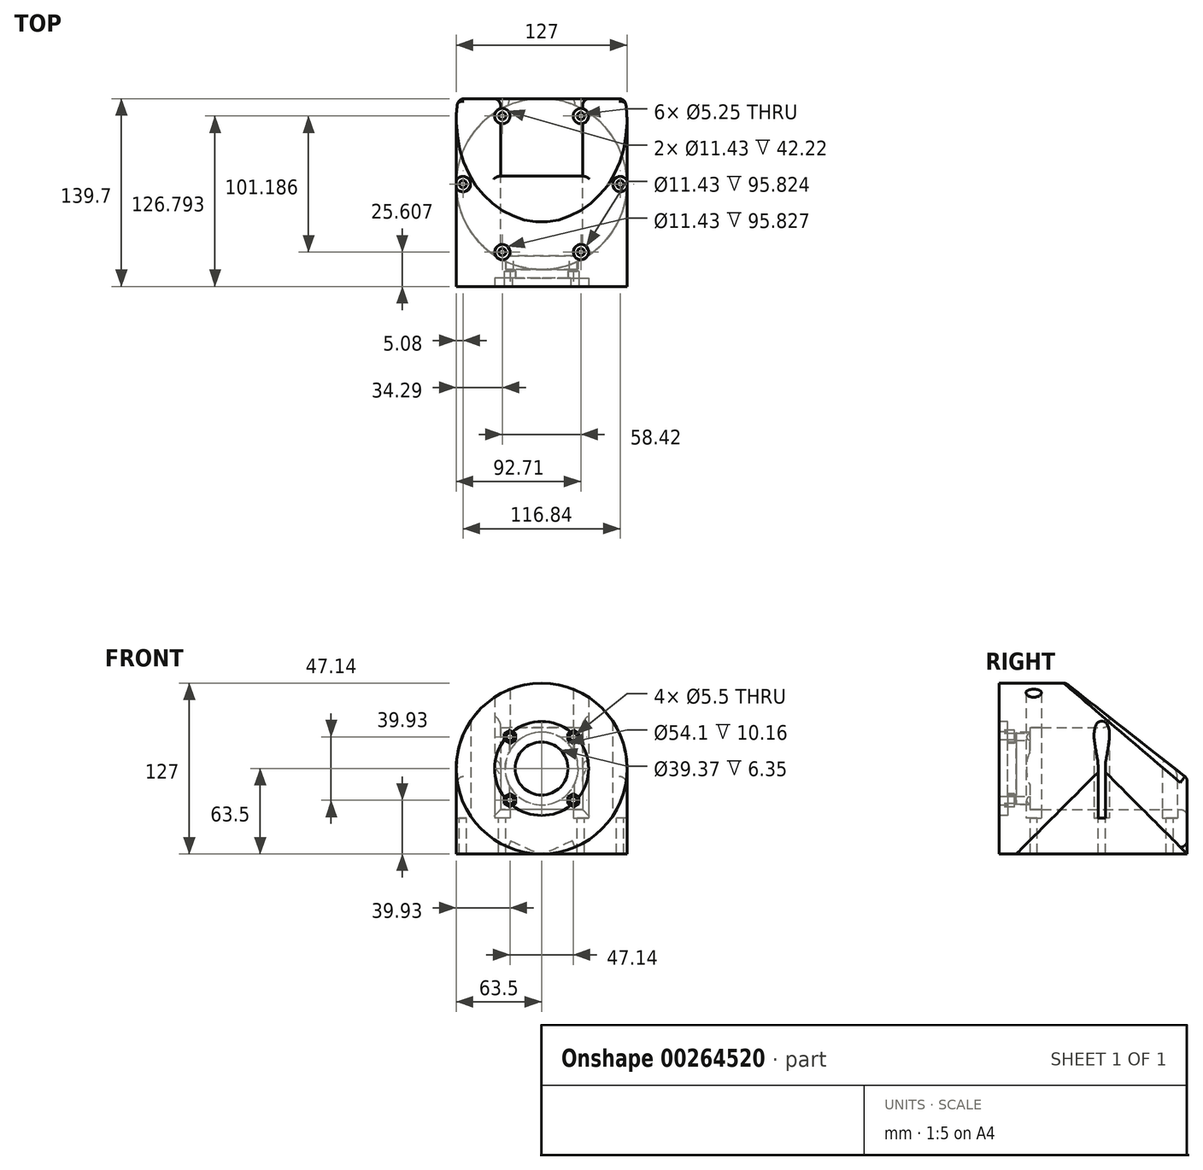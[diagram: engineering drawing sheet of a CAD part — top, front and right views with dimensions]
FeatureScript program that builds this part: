
annotation { "Feature Type Name" : "Feature", "Feature Type Description" : "" }
export const myFeature = defineFeature(function(context is Context, id is Id, definition is map)
    precondition{}
    {
        {
            var Q0;
            Q0=qCreatedBy(makeId("Front.planeOp"),FACE);
            var sketch = newSketch(context, id + "F0", { "sketchPlane" : qUnion([Q0])});
            skCircle(sketch, "E0", {"center": v(0, 0) * mm, "radius": 63.5 * mm});
            skSolve(sketch);
        }
        {
            var Q0;
            Q0 = qSketchRegion(id + "F0", true);
            extrude(context, id + "F1", {"entities" : qUnion([Q0]), "depth" : 76.2 * mm, "hasSecondDirection" : true, "secondDirectionOppositeDirection" : true, "secondDirectionDepth" : 63.5 * mm});
        }
        {
            var Q0;
            Q0=qCreatedBy(makeId("Top.planeOp"),FACE);
            var sketch = newSketch(context, id + "F2", { "sketchPlane" : qUnion([Q0])});
            skCircle(sketch, "E1", {"center": v(0, 0) * mm, "radius": 63.5 * mm});
            skSolve(sketch);
        }
        {
            var Q0;
            Q0 = qSketchRegion(id + "F2", true);
            extrude(context, id + "F3", {"entities" : qUnion([Q0]), "operationType" : NewBodyOperationType.ADD, "oppositeDirection" : true, "depth" : 63.5 * mm});
        }
        {
            var Q0;
            Q0=makeQuery(id+"F1.opExtrude","CAP_FACE",FACE,{"disambiguationData":[OSD([sQuery(id+"F0.wireOp",EDGE,"E0")])],"isStart":true});
            var sketch = newSketch(context, id + "F4", { "sketchPlane" : qUnion([Q0])});
            skLineSegment(sketch, "E2.bottom", {"start": v(-30.48, 30.48) * mm, "end": v(30.48, 30.48) * mm});
            skLineSegment(sketch, "E2.top", {"start": v(-30.48, -30.48) * mm, "end": v(30.48, -30.48) * mm});
            skLineSegment(sketch, "E2.left", {"start": v(-30.48, 30.48) * mm, "end": v(-30.48, -30.48) * mm});
            skLineSegment(sketch, "E2.right", {"start": v(30.48, 30.48) * mm, "end": v(30.48, -30.48) * mm});
            skPoint(sketch, "E2.middle", {"position": v(0, 0) * mm});
            skSolve(sketch);
        }
        {
            var Q0;
            Q0 = qSketchRegion(id + "F4", true);
            extrude(context, id + "F5", {"entities" : qUnion([Q0]), "operationType" : NewBodyOperationType.REMOVE, "oppositeDirection" : true, "depth" : 127 * mm});
        }
        {
            var Q0;
            Q0=makeQuery(id+"F1.opExtrude","CAP_FACE",FACE,{"disambiguationData":[OSD([sQuery(id+"F0.wireOp",EDGE,"E0")])],"isStart":false});
            var sketch = newSketch(context, id + "F6", { "sketchPlane" : qUnion([Q0])});
            skCircle(sketch, "E3", {"center": v(0, 0) * mm, "radius": 34.93 * mm});
            skSolve(sketch);
        }
        {
            var Q0;
            Q0 = qSketchRegion(id + "F6", true);
            extrude(context, id + "F7", {"entities" : qUnion([Q0]), "operationType" : NewBodyOperationType.REMOVE, "oppositeDirection" : true, "depth" : 6.35 * mm});
        }
        {
            var Q0;
            Q0=makeQuery(id+"F7.boolean.opBoolean","COPY",FACE,{"derivedFrom":makeQuery(id+"F7.opExtrude","CAP_FACE",FACE,{"disambiguationData":[OSD([sQuery(id+"F6.wireOp",EDGE,"E3")])],"isStart":false})});
            var sketch = newSketch(context, id + "F8", { "sketchPlane" : qUnion([Q0])});
            skCircle(sketch, "E4", {"center": v(0, 0) * mm, "radius": 19.69 * mm});
            skSolve(sketch);
        }
        {
            var Q0;
            Q0 = qSketchRegion(id + "F8", true);
            extrude(context, id + "F9", {"entities" : qUnion([Q0]), "operationType" : NewBodyOperationType.REMOVE, "endBound" : BoundingType.THROUGH_ALL, "oppositeDirection" : true, "depth" : 25.4 * mm});
        }
        {
            var Q0;
            Q0=makeQuery(id+"F5.boolean.opBoolean","COPY",FACE,{"derivedFrom":makeQuery(id+"F5.opExtrude","CAP_FACE",FACE,{"disambiguationData":[OSD([sQuery(id+"F4.wireOp",EDGE,"E2.bottom"),sQuery(id+"F4.wireOp",EDGE,"E2.top"),sQuery(id+"F4.wireOp",EDGE,"E2.left"),sQuery(id+"F4.wireOp",EDGE,"E2.right")])],"isStart":false})});
            var sketch = newSketch(context, id + "F10", { "sketchPlane" : qUnion([Q0])});
            skLineSegment(sketch, "E5.bottom", {"start": v(30.48, 30.48) * mm, "end": v(-30.48, 30.48) * mm});
            skLineSegment(sketch, "E5.top", {"start": v(30.48, -30.48) * mm, "end": v(-30.48, -30.48) * mm});
            skLineSegment(sketch, "E5.left", {"start": v(30.48, 30.48) * mm, "end": v(30.48, -30.48) * mm});
            skLineSegment(sketch, "E5.right", {"start": v(-30.48, 30.48) * mm, "end": v(-30.48, -30.48) * mm});
            skPoint(sketch, "E5.middle", {"position": v(0, 0) * mm});
            skCircle(sketch, "E6", {"center": v(0, 0) * mm, "radius": 27.05 * mm});
            skSolve(sketch);
        }
        {
            var Q0;
            Q0 = qSketchRegion(id + "F10", true);
            extrude(context, id + "F11", {"entities" : qUnion([Q0]), "operationType" : NewBodyOperationType.ADD, "depth" : 10.16 * mm});
        }
        {
            var Q0;
            Q0=qCreatedBy(makeId("Right.planeOp"),FACE);
            var sketch = newSketch(context, id + "F12", { "sketchPlane" : qUnion([Q0])});
            skLineSegment(sketch, "E7", {"start": v(64.02, -7.62) * mm, "end": v(-26.67, 63.5) * mm});
            skLineSegment(sketch, "E8", {"start": v(-26.67, 63.5) * mm, "end": v(64.02, 63.5) * mm});
            skLineSegment(sketch, "E9", {"start": v(64.02, 63.5) * mm, "end": v(64.02, -7.62) * mm});
            skLineSegment(sketch, "E10", {"start": v(-26.67, 0) * mm, "end": v(0, 0) * mm, "construction": true});
            skLineSegment(sketch, "E11", {"start": v(-26.67, 63.5) * mm, "end": v(-26.67, 0) * mm, "construction": true});
            skSolve(sketch);
        }
        {
            var Q0;
            Q0 = qSketchRegion(id + "F12", true);
            extrude(context, id + "F13", {"entities" : qUnion([Q0]), "operationType" : NewBodyOperationType.REMOVE, "endBound" : BoundingType.THROUGH_ALL, "oppositeDirection" : true, "depth" : 25.4 * mm, "hasSecondDirection" : true, "secondDirectionBound" : BoundingType.THROUGH_ALL, "secondDirectionOppositeDirection" : false, "secondDirectionDepth" : 25.4 * mm});
        }
        {
            var Q0;
            Q0=makeQuery(id+"F13.boolean.opBoolean","COPY",FACE,{"derivedFrom":makeQuery(id+"F13.opExtrude","SWEPT_FACE",FACE,{"disambiguationData":[OSD([sQuery(id+"F12.wireOp",EDGE,"E7")])]})});
            var Q1;
            Q1=makeQuery(id+"F1.opExtrude","CAP_FACE",FACE,{"disambiguationData":[OSD([sQuery(id+"F0.wireOp",EDGE,"E0")])],"isStart":true});
            fillet(context, id + "F14", {"entities" : qUnion([Q0, Q1]), "radius" : 5.08 * mm, "tangentPropagation" : true, "allowEdgeOverflow" : false});
        }
        {
            var Q0;
            Q0=makeQuery(id+"F1.opExtrude","CAP_FACE",FACE,{"disambiguationData":[OSD([sQuery(id+"F0.wireOp",EDGE,"E0")])],"isStart":false});
            var sketch = newSketch(context, id + "F15", { "sketchPlane" : qUnion([Q0])});
            skLineSegment(sketch, "E12.bottom", {"start": v(23.57, 23.57) * mm, "end": v(-23.57, 23.57) * mm, "construction": true});
            skLineSegment(sketch, "E12.top", {"start": v(23.57, -23.57) * mm, "end": v(-23.57, -23.57) * mm, "construction": true});
            skLineSegment(sketch, "E12.left", {"start": v(23.57, 23.57) * mm, "end": v(23.57, -23.57) * mm, "construction": true});
            skLineSegment(sketch, "E12.right", {"start": v(-23.57, 23.57) * mm, "end": v(-23.57, -23.57) * mm, "construction": true});
            skPoint(sketch, "E12.middle", {"position": v(0, 0) * mm});
            skPoint(sketch, "E13", {"position": v(-23.57, 23.57) * mm});
            skPoint(sketch, "E14", {"position": v(23.57, 23.57) * mm});
            skPoint(sketch, "E15", {"position": v(23.57, -23.57) * mm});
            skPoint(sketch, "E16", {"position": v(-23.57, -23.57) * mm});
            skSolve(sketch);
        }
        {
            var Q0;
            Q0=sQuery(id+"F15.wireOp",VERTEX,"E13");
            var Q1;
            Q1=sQuery(id+"F15.wireOp",VERTEX,"E16");
            var Q2;
            Q2=sQuery(id+"F15.wireOp",VERTEX,"E15");
            var Q3;
            Q3=sQuery(id+"F15.wireOp",VERTEX,"E14");
            var Q4;
            Q4=makeQuery(id+"F1.opExtrude","SWEPT_BODY",BODY,{"disambiguationData":[OSD([sQuery(id+"F0.wireOp",EDGE,"E0")])]});
            hole(context, id + "F16", {"style" : HoleStyle.SIMPLE, "endStyle" : HoleEndStyle.THROUGH, "holeDiameter" : 5.5 * mm, "tappedDepth" : 12.7 * mm, "tapClearance" : 3, "locations" : qUnion([Q0, Q1, Q2, Q3]), "scope" : qUnion([Q4]), "startStyle" : HoleStartStyle.PART});
        }
        {
            var Q0;
            Q0=makeQuery(id+"F7.boolean.opBoolean","COPY",FACE,{"derivedFrom":makeQuery(id+"F7.opExtrude","CAP_FACE",FACE,{"disambiguationData":[OSD([sQuery(id+"F6.wireOp",EDGE,"E3")])],"isStart":false})});
            var sketch = newSketch(context, id + "F17", { "sketchPlane" : qUnion([Q0])});
            skLineSegment(sketch, "E17.bottom", {"start": v(-23.57, 23.57) * mm, "end": v(23.57, 23.57) * mm, "construction": true});
            skLineSegment(sketch, "E17.top", {"start": v(-23.57, -23.57) * mm, "end": v(23.57, -23.57) * mm, "construction": true});
            skLineSegment(sketch, "E17.left", {"start": v(-23.57, 23.57) * mm, "end": v(-23.57, -23.57) * mm, "construction": true});
            skLineSegment(sketch, "E17.right", {"start": v(23.57, 23.57) * mm, "end": v(23.57, -23.57) * mm, "construction": true});
            skPoint(sketch, "E17.middle", {"position": v(0, 0) * mm});
            skCircle(sketch, "E18.cCircle", {"center": v(-23.57, 23.57) * mm, "radius": 4.25 * mm, "construction": true});
            skLineSegment(sketch, "E18.0", {"start": v(-27.82, 26.02) * mm, "end": v(-23.57, 28.48) * mm});
            skLineSegment(sketch, "E18.1", {"start": v(-23.57, 28.48) * mm, "end": v(-19.32, 26.02) * mm});
            skLineSegment(sketch, "E18.2", {"start": v(-19.32, 26.02) * mm, "end": v(-19.32, 21.12) * mm});
            skLineSegment(sketch, "E18.3", {"start": v(-19.32, 21.12) * mm, "end": v(-23.57, 18.66) * mm});
            skLineSegment(sketch, "E18.4", {"start": v(-23.57, 18.66) * mm, "end": v(-27.82, 21.12) * mm});
            skLineSegment(sketch, "E18.5", {"start": v(-27.82, 21.12) * mm, "end": v(-27.82, 26.02) * mm});
            skPoint(sketch, "E18.0.midPoint", {"position": v(-25.7, 27.25) * mm});
            skCircle(sketch, "E19.cCircle", {"center": v(23.57, 23.57) * mm, "radius": 4.25 * mm, "construction": true});
            skLineSegment(sketch, "E19.0", {"start": v(19.32, 26.02) * mm, "end": v(23.57, 28.48) * mm});
            skLineSegment(sketch, "E19.1", {"start": v(23.57, 28.48) * mm, "end": v(27.82, 26.02) * mm});
            skLineSegment(sketch, "E19.2", {"start": v(27.82, 26.02) * mm, "end": v(27.82, 21.12) * mm});
            skLineSegment(sketch, "E19.3", {"start": v(27.82, 21.12) * mm, "end": v(23.57, 18.66) * mm});
            skLineSegment(sketch, "E19.4", {"start": v(23.57, 18.66) * mm, "end": v(19.32, 21.12) * mm});
            skLineSegment(sketch, "E19.5", {"start": v(19.32, 21.12) * mm, "end": v(19.32, 26.02) * mm});
            skPoint(sketch, "E19.0.midPoint", {"position": v(21.45, 27.25) * mm});
            skCircle(sketch, "E20.cCircle", {"center": v(23.57, -23.57) * mm, "radius": 4.25 * mm, "construction": true});
            skLineSegment(sketch, "E20.0", {"start": v(23.57, -18.66) * mm, "end": v(27.82, -21.12) * mm});
            skLineSegment(sketch, "E20.1", {"start": v(27.82, -21.12) * mm, "end": v(27.82, -26.02) * mm});
            skLineSegment(sketch, "E20.2", {"start": v(27.82, -26.02) * mm, "end": v(23.57, -28.48) * mm});
            skLineSegment(sketch, "E20.3", {"start": v(23.57, -28.48) * mm, "end": v(19.32, -26.02) * mm});
            skLineSegment(sketch, "E20.4", {"start": v(19.32, -26.02) * mm, "end": v(19.32, -21.12) * mm});
            skLineSegment(sketch, "E20.5", {"start": v(19.32, -21.12) * mm, "end": v(23.57, -18.66) * mm});
            skPoint(sketch, "E20.0.midPoint", {"position": v(25.7, -19.89) * mm});
            skCircle(sketch, "E21.cCircle", {"center": v(-23.57, -23.57) * mm, "radius": 4.25 * mm, "construction": true});
            skLineSegment(sketch, "E21.0", {"start": v(-23.57, -18.66) * mm, "end": v(-19.32, -21.12) * mm});
            skLineSegment(sketch, "E21.1", {"start": v(-19.32, -21.12) * mm, "end": v(-19.32, -26.02) * mm});
            skLineSegment(sketch, "E21.2", {"start": v(-19.32, -26.02) * mm, "end": v(-23.57, -28.48) * mm});
            skLineSegment(sketch, "E21.3", {"start": v(-23.57, -28.48) * mm, "end": v(-27.82, -26.02) * mm});
            skLineSegment(sketch, "E21.4", {"start": v(-27.82, -26.02) * mm, "end": v(-27.82, -21.12) * mm});
            skLineSegment(sketch, "E21.5", {"start": v(-27.82, -21.12) * mm, "end": v(-23.57, -18.66) * mm});
            skPoint(sketch, "E21.0.midPoint", {"position": v(-21.45, -19.89) * mm});
            skSolve(sketch);
        }
        {
            var Q0;
            Q0 = qSketchRegion(id + "F17", true);
            var Q1;
            Q1=makeQuery(id+"F1.opExtrude","CAP_FACE",FACE,{"disambiguationData":[OSD([sQuery(id+"F0.wireOp",EDGE,"E0")])],"isStart":false});
            extrude(context, id + "F18", {"entities" : qUnion([Q0]), "operationType" : NewBodyOperationType.REMOVE, "oppositeDirection" : true, "depth" : 5 * mm, "hasSecondDirection" : true, "secondDirectionBound" : BoundingType.UP_TO_SURFACE, "secondDirectionOppositeDirection" : false, "secondDirectionBoundEntityFace" : qUnion([Q1]), "secondDirectionDepth" : 25.4 * mm});
        }
        {
            var Q0;
            Q0=makeQuery(id+"F3.opExtrude","CAP_FACE",FACE,{"disambiguationData":[OSD([sQuery(id+"F2.wireOp",EDGE,"E1")])],"isStart":false});
            var sketch = newSketch(context, id + "F19", { "sketchPlane" : qUnion([Q0])});
            skCircle(sketch, "E22.cCircle", {"center": v(0, 0) * mm, "radius": 58.42 * mm, "construction": true});
            skLineSegment(sketch, "E22.0", {"start": v(-29.2, -50.6) * mm, "end": v(-58.42, 0) * mm, "construction": true});
            skLineSegment(sketch, "E22.1", {"start": v(-58.42, 0) * mm, "end": v(-29.21, 50.6) * mm, "construction": true});
            skLineSegment(sketch, "E22.2", {"start": v(-29.21, 50.6) * mm, "end": v(29.21, 50.6) * mm, "construction": true});
            skLineSegment(sketch, "E22.3", {"start": v(29.2, 50.6) * mm, "end": v(58.42, 0) * mm, "construction": true});
            skLineSegment(sketch, "E22.4", {"start": v(58.42, 0) * mm, "end": v(29.21, -50.6) * mm, "construction": true});
            skLineSegment(sketch, "E22.5", {"start": v(29.2, -50.6) * mm, "end": v(-29.21, -50.6) * mm, "construction": true});
            skSolve(sketch);
        }
        {
            var Q0;
            Q0=sQuery(id+"F19.wireOp",VERTEX,"E22.1.start");
            var Q1;
            Q1=sQuery(id+"F19.wireOp",VERTEX,"E22.5.end");
            var Q2;
            Q2=sQuery(id+"F19.wireOp",VERTEX,"E22.5.start");
            var Q3;
            Q3=sQuery(id+"F19.wireOp",VERTEX,"E22.2.start");
            var Q4;
            Q4=sQuery(id+"F19.wireOp",VERTEX,"E22.4.start");
            var Q5;
            Q5=sQuery(id+"F19.wireOp",VERTEX,"E22.3.start");
            var Q6;
            Q6=makeQuery(id+"F1.opExtrude","SWEPT_BODY",BODY,{"disambiguationData":[OSD([sQuery(id+"F0.wireOp",EDGE,"E0")])]});
            hole(context, id + "F20", {"style" : HoleStyle.SIMPLE, "endStyle" : HoleEndStyle.THROUGH, "standardTappedOrClearance" : lookupTablePath({ "fit" : "Close", "standard" : "ISO", "size" : "M5", "type" : "Clearance" }), "standardBlindInLast" : lookupTablePath({ "fit" : "Close", "standard" : "ISO", "size" : "M5", "type" : "Clearance" }), "holeDiameter" : 5.25 * mm, "tappedDepth" : 12.7 * mm, "tapClearance" : 3, "locations" : qUnion([Q0, Q1, Q2, Q3, Q4, Q5]), "scope" : qUnion([Q6]), "startStyle" : HoleStartStyle.PART});
        }
        {
            var Q0;
            Q0=makeQuery(id+"F5.boolean.opBoolean","COPY",FACE,{"derivedFrom":makeQuery(id+"F5.opExtrude","SWEPT_FACE",FACE,{"disambiguationData":[OSD([sQuery(id+"F4.wireOp",EDGE,"E2.top")])]})});
            var sketch = newSketch(context, id + "F21", { "sketchPlane" : qUnion([Q0])});
            skPoint(sketch, "E23", {"position": v(29.2, 50.6) * mm});
            skPoint(sketch, "E24", {"position": v(58.42, 0) * mm});
            skPoint(sketch, "E25", {"position": v(29.2, -50.6) * mm});
            skPoint(sketch, "E26", {"position": v(-29.21, -50.6) * mm});
            skPoint(sketch, "E27", {"position": v(-58.42, 0) * mm});
            skPoint(sketch, "E28", {"position": v(-29.21, 50.6) * mm});
            skCircle(sketch, "E29", {"center": v(58.42, 0) * mm, "radius": 5.72 * mm});
            skCircle(sketch, "E30.1.0", {"center": v(29.21, 50.6) * mm, "radius": 5.72 * mm});
            skCircle(sketch, "E30.2.0", {"center": v(-29.2, 50.6) * mm, "radius": 5.72 * mm});
            skCircle(sketch, "E30.3.0", {"center": v(-58.42, 0) * mm, "radius": 5.72 * mm});
            skCircle(sketch, "E30.4.0", {"center": v(-29.21, -50.6) * mm, "radius": 5.72 * mm});
            skCircle(sketch, "E30.5.0", {"center": v(29.2, -50.6) * mm, "radius": 5.72 * mm});
            skPoint(sketch, "E30.center", {"position": v(0, 0) * mm});
            skSolve(sketch);
        }
        {
            var Q0;
            Q0 = qSketchRegion(id + "F21", true);
            extrude(context, id + "F22", {"entities" : qUnion([Q0]), "operationType" : NewBodyOperationType.REMOVE, "endBound" : BoundingType.THROUGH_ALL, "depth" : 25.4 * mm, "hasSecondDirection" : true, "secondDirectionOppositeDirection" : true, "secondDirectionDepth" : 6.35 * mm});
        }
    });
